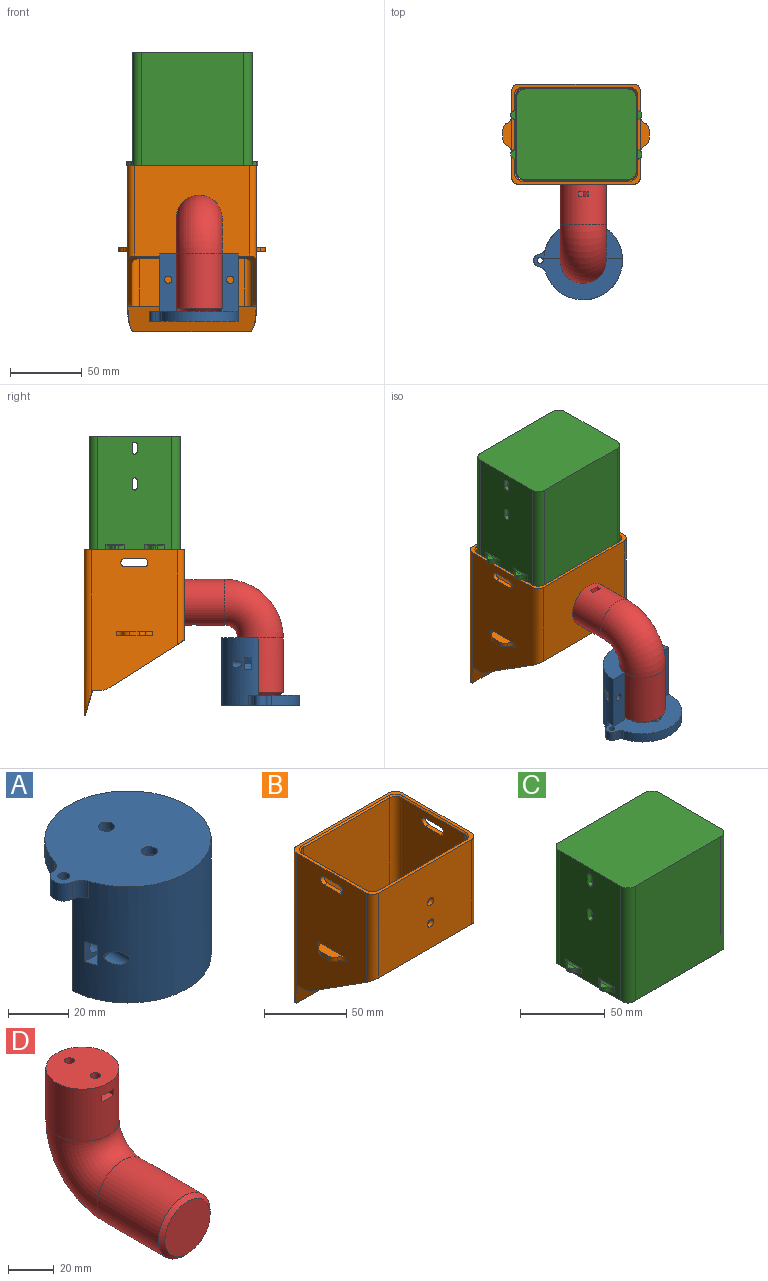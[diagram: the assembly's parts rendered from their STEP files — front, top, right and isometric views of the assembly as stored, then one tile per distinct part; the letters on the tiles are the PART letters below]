
ASSEMBLY  parts=4 mates=7
PART A: 33 faces, bbox 62x55x47 mm
  f0: cylinder r=27.5mm len=55mm, axis (0,0,-1), area 4287.3mm2, adj f1,f2,f6,f7,f8,f9,f10,f17
  f1: cylinder r=2.6mm len=8.99mm, axis (0,1,0), area 95.2mm2, adj f0,f25
  f2: cylinder r=2.6mm len=8.99mm, axis (0,1,0), area 95.1mm2, adj f0,f19
  f3: cylinder r=2.65mm len=5.3mm, axis (0,0,-1), area 50mm2, adj f8,f14
  f4: cylinder r=2.65mm len=5.3mm, axis (0,0,-1), area 50mm2, adj f8,f12
  f5: cylinder r=16mm len=40mm, axis (0,0,-1), area 1890.4mm2, adj f6,f7,f9,f10
  f6: plane 54.92x26mm, normal (0,0,-1), area 751.3mm2, adj f0,f5,f9,f10
  f7: plane 62x43.5mm, normal (0,0,-1), area 1446.6mm2, adj f0,f5,f9,f10,f11,f13,f29,f30
  f8: plane 62x55mm, normal (0,0,1), area 2379.9mm2, adj f0,f3,f4,f29,f30,f31,f32
  f9: plane 40x11.53mm, normal (0,1,0), area 439.9mm2, adj f0,f5,f6,f7,f16
  f10: plane 40x11.53mm, normal (0,1,0), area 439.9mm2, adj f0,f5,f6,f7,f15
  f11: cylinder r=6mm len=12mm, axis (0,0,-1), area 150.8mm2, adj f7,f12
  f12: plane 12x12mm, normal (0,0,-1), area 91mm2, adj f4,f11
  f13: cylinder r=6mm len=12mm, axis (0,0,-1), area 150.8mm2, adj f7,f14
  f14: plane 12x12mm, normal (0,0,-1), area 91mm2, adj f3,f13
  f15: cylinder r=2.6mm len=5.2mm, axis (0,1,0), area 81.7mm2, adj f10,f20
  f16: cylinder r=2.6mm len=5.2mm, axis (0,1,0), area 81.7mm2, adj f9,f26
  f17: plane 7.38x4.3mm, normal (0,0,-1), area 28.9mm2, adj f0,f19,f20,f21
  f18: plane 7.38x4.3mm, normal (0,0,1), area 28.9mm2, adj f0,f19,f20,f22
  f19: plane 8.3x8.15mm, normal (0,1,0), area 36.8mm2, adj f0,f2,f17,f18,f21,f22
  f20: plane 9.73x8.15mm, normal (0,-1,0), area 48.5mm2, adj f0,f15,f17,f18,f21,f22
  f21: plane 4.3x4.08mm, normal (-0.87,0,-0.5), area 20.2mm2, adj f17,f19,f20,f22
  f22: plane 4.3x4.08mm, normal (-0.87,0,0.5), area 20.2mm2, adj f18,f19,f20,f21
  f23: plane 7.38x4.3mm, normal (0,0,-1), area 28.9mm2, adj f0,f25,f26,f28
  f24: plane 7.38x4.3mm, normal (0,0,1), area 28.9mm2, adj f0,f25,f26,f27
  f25: plane 8.3x8.15mm, normal (0,1,0), area 36.8mm2, adj f0,f1,f23,f24,f27,f28
  f26: plane 9.73x8.15mm, normal (0,-1,0), area 48.5mm2, adj f0,f16,f23,f24,f27,f28
  f27: plane 4.3x4.08mm, normal (0.87,0,0.5), area 20.2mm2, adj f24,f25,f26,f28
  f28: plane 4.3x4.08mm, normal (0.87,0,-0.5), area 20.2mm2, adj f23,f25,f26,f27
  f29: cylinder r=4.5mm len=8.94mm, axis (0,0,-1), area 91.6mm2, adj f7,f8,f31,f32
  f30: cylinder r=2mm len=7mm, axis (0,0,-1), area 88mm2, adj f7,f8
  f31: cylinder r=5mm len=7mm, axis (0,0,1), area 40.6mm2, adj f0,f7,f8,f29
  f32: cylinder r=5mm len=7mm, axis (0,0,1), area 40.6mm2, adj f0,f7,f8,f29
PART B: 61 faces, bbox 103.3x71.3x117.4 mm
  f0: plane 97x54mm, normal (-1,0,0), area 4428.1mm2, adj f5,f11,f18,f19,f22,f33,f34,f35
  f1: plane 100.31x60mm, normal (1,0,0), area 4903.3mm2, adj f5,f10,f11,f14,f17,f22,f26,f33
  f2: plane 100.31x60mm, normal (-1,0,0), area 4903.3mm2, adj f4,f10,f11,f15,f16,f23,f30,f31
  f3: plane 97x54mm, normal (1,0,0), area 4428.1mm2, adj f4,f11,f20,f21,f23,f31,f32,f37
  f4: plane 6.39x3.42mm, normal (0,0,-1), area 18.6mm2, adj f2,f3,f13,f21,f23,f30
  f5: plane 6.39x3.42mm, normal (0,0,-1), area 18.6mm2, adj f0,f1,f13,f18,f22,f26
  f6: plane 80x63mm, normal (0,-1,0), area 4992.5mm2, adj f10,f11,f16,f17,f24,f25
  f7: plane 97x74mm, normal (0,-1,0), area 7178mm2, adj f12,f18,f21,f46
  f8: plane 74x63.91mm, normal (0,1,0), area 4681.8mm2, adj f11,f19,f20,f24,f25,f39
  f9: plane 116x80mm, normal (0,1,0), area 9280mm2, adj f10,f14,f15,f28
  f10: plane 90x70mm, normal (0,0,1), area 633.4mm2, adj f1,f2,f6,f9,f14,f15,f16,f17
  f11: plane 91.34x53.88mm, normal (0,-0.54,-0.84), area 672.4mm2, adj f0,f1,f2,f3,f6,f8,f16,f17
  f12: plane 83.17x3mm, normal (0,0,1), area 241.8mm2, adj f7,f13,f18,f21
  f13: plane 89.43x18.1mm, normal (0,-0.96,-0.29), area 1655.1mm2, adj f4,f5,f12,f26,f27,f28,f29,f30
  f14: cylinder r=5mm len=116mm, axis (0,0,1), area 849.5mm2, adj f1,f9,f10,f27
  f15: cylinder r=5mm len=116mm, axis (0,0,-1), area 849.5mm2, adj f2,f9,f10,f29
  f16: cylinder r=5mm len=66.18mm, axis (0,0,1), area 507.3mm2, adj f2,f6,f10,f11
  f17: cylinder r=5mm len=66.18mm, axis (0,0,-1), area 507.3mm2, adj f1,f6,f10,f11
  f18: cylinder r=5mm len=97mm, axis (0,0,-1), area 761.8mm2, adj f0,f5,f7,f12,f44
  f19: cylinder r=5mm len=67.09mm, axis (0,0,1), area 514.4mm2, adj f0,f8,f11,f40
  f20: cylinder r=5mm len=67.09mm, axis (0,0,-1), area 514.4mm2, adj f3,f8,f11,f41
  f21: cylinder r=5mm len=97mm, axis (0,0,1), area 761.8mm2, adj f3,f4,f7,f12,f45
  f22: cylinder r=10mm len=5.37mm, axis (-1,0,0), area 17mm2, adj f0,f1,f5,f11
  f23: cylinder r=10mm len=5.37mm, axis (-1,0,0), area 17mm2, adj f2,f3,f4,f11
  f24: cylinder r=2.75mm len=5.5mm, axis (0,-1,0), area 51.8mm2, adj f6,f8
  f25: cylinder r=2.75mm len=5.5mm, axis (0,-1,0), area 51.8mm2, adj f6,f8
  f26: plane 2.4x1mm, normal (0.71,-0.68,-0.2), area 1mm2, adj f1,f5,f13,f27
  f27: bspline ~15.77x5.28mm, area 9.1mm2, adj f13,f14,f26,f28
  f28: plane 80x0.57mm, normal (0,0.15,-0.99), area 46.5mm2, adj f9,f13,f27,f29
  f29: bspline ~15.77x5.28mm, area 9.1mm2, adj f13,f15,f28,f30
  f30: plane 2.4x1mm, normal (-0.71,-0.68,-0.2), area 1mm2, adj f2,f4,f13,f29
  f31: plane 13x3mm, normal (0,0,1), area 39mm2, adj f2,f3,f37,f38
  f32: plane 13x3mm, normal (0,0,-1), area 39mm2, adj f2,f3,f37,f38
  f33: plane 13x3mm, normal (0,0,-1), area 39mm2, adj f0,f1,f35,f36
  f34: plane 13x3mm, normal (0,0,1), area 39mm2, adj f0,f1,f35,f36
  f35: cylinder r=3mm len=6mm, axis (-1,0,0), area 28.3mm2, adj f0,f1,f33,f34
  f36: cylinder r=3mm len=6mm, axis (1,0,0), area 28.3mm2, adj f0,f1,f33,f34
  f37: cylinder r=3mm len=6mm, axis (-1,0,0), area 28.3mm2, adj f2,f3,f31,f32
  f38: cylinder r=3mm len=6mm, axis (-1,0,0), area 28.3mm2, adj f2,f3,f31,f32
  f39: plane 74x1mm, normal (0,0.71,0.71), area 104.7mm2, adj f8,f10,f40,f41
  f40: cone r=6mm half-angle=45deg, axis (0,0,1), area 12.2mm2, adj f10,f19,f39,f42
  f41: cone r=6mm half-angle=45deg, axis (0,0,1), area 12.2mm2, adj f10,f20,f39,f43
  f42: plane 54x1mm, normal (-0.71,0,0.71), area 76.4mm2, adj f0,f10,f40,f44
  f43: plane 54x1mm, normal (0.71,0,0.71), area 76.4mm2, adj f3,f10,f41,f45
  f44: cone r=6mm half-angle=45deg, axis (0,0,1), area 12.2mm2, adj f10,f18,f42,f46
  f45: cone r=6mm half-angle=45deg, axis (0,0,1), area 12.2mm2, adj f10,f21,f43,f46
  f46: plane 74x1mm, normal (0,-0.71,0.71), area 104.7mm2, adj f7,f10,f44,f45
  f47: plane 6.67x3mm, normal (-1,0,0), area 20mm2, adj f48,f49,f52,f53
  f48: plane 25x6mm, normal (0,0,1), area 95mm2, adj f2,f47,f50,f51,f52,f53
  f49: plane 25x6mm, normal (0,0,-1), area 95mm2, adj f2,f47,f50,f51,f52,f53
  f50: cylinder r=5mm len=4.58mm, axis (0,0,1), area 17.4mm2, adj f2,f48,f49,f52
  f51: cylinder r=5mm len=4.58mm, axis (0,0,-1), area 17.4mm2, adj f2,f48,f49,f53
  f52: cylinder r=5mm len=4.58mm, axis (0,0,1), area 17.4mm2, adj f47,f48,f49,f50
  f53: cylinder r=5mm len=4.58mm, axis (0,0,-1), area 17.4mm2, adj f47,f48,f49,f51
  f54: plane 6.67x3mm, normal (1,0,0), area 20mm2, adj f55,f56,f59,f60
  f55: plane 25x6mm, normal (0,0,1), area 95mm2, adj f1,f54,f57,f58,f59,f60
  f56: plane 25x6mm, normal (0,0,-1), area 95mm2, adj f1,f54,f57,f58,f59,f60
  f57: cylinder r=5mm len=4.58mm, axis (0,0,1), area 17.4mm2, adj f1,f55,f56,f59
  f58: cylinder r=5mm len=4.58mm, axis (0,0,-1), area 17.4mm2, adj f1,f55,f56,f60
  f59: cylinder r=5mm len=4.58mm, axis (0,0,1), area 17.4mm2, adj f54,f55,f56,f57
  f60: cylinder r=5mm len=4.58mm, axis (0,0,-1), area 17.4mm2, adj f54,f55,f56,f58
PART C: 75 faces, bbox 91.5x63.5x84.5 mm
  f0: plane 82.5x51.5mm, normal (1,0,0), area 4084.1mm2, adj f10,f15,f18,f27,f28,f29,f30,f31
  f1: plane 82.5x51.5mm, normal (-1,0,0), area 4084.1mm2, adj f10,f16,f17,f19,f20,f21,f22,f23
  f2: plane 81.5x49.5mm, normal (1,0,0), area 3980mm2, adj f8,f9,f11,f14,f19,f20,f21,f22
  f3: plane 81.5x69.5mm, normal (0,-1,0), area 5664.3mm2, adj f8,f9,f11,f12
  f4: plane 81.5x49.5mm, normal (-1,0,0), area 3980mm2, adj f8,f9,f12,f13,f27,f28,f29,f30
  f5: plane 82.5x71.5mm, normal (0,1,0), area 5898.7mm2, adj f10,f15,f16,f67
  f6: plane 82.5x71.5mm, normal (0,-1,0), area 5898.7mm2, adj f10,f17,f18,f74
  f7: plane 81.5x69.5mm, normal (0,1,0), area 5664.3mm2, adj f8,f9,f13,f14
  f8: plane 79.5x59.5mm, normal (0,0,-1), area 274mm2, adj f2,f3,f4,f7,f11,f12,f13,f14
  f9: plane 77.5x57.5mm, normal (0,0,-1), area 4442.5mm2, adj f2,f3,f4,f7,f11,f12,f13,f14
  f10: plane 83.5x63.5mm, normal (0,0,1), area 5271.3mm2, adj f0,f1,f5,f6,f15,f16,f17,f18
  f11: cylinder r=4mm len=81.5mm, axis (0,0,1), area 512.1mm2, adj f2,f3,f8,f9
  f12: cylinder r=4mm len=81.5mm, axis (0,0,-1), area 512.1mm2, adj f3,f4,f8,f9
  f13: cylinder r=4mm len=81.5mm, axis (0,0,1), area 512.1mm2, adj f4,f7,f8,f9
  f14: cylinder r=4mm len=81.5mm, axis (0,0,-1), area 512.1mm2, adj f2,f7,f8,f9
  f15: cylinder r=6mm len=82.5mm, axis (0,0,1), area 777.5mm2, adj f0,f5,f10,f68
  f16: cylinder r=6mm len=82.5mm, axis (0,0,-1), area 777.5mm2, adj f1,f5,f10,f69
  f17: cylinder r=6mm len=82.5mm, axis (0,0,1), area 777.5mm2, adj f1,f6,f10,f73
  f18: cylinder r=6mm len=82.5mm, axis (0,0,-1), area 777.5mm2, adj f0,f6,f10,f72
  f19: plane 5x3mm, normal (0,1,0), area 15mm2, adj f1,f2,f20,f22
  f20: cylinder r=1.75mm len=3.5mm, axis (1,0,0), area 16.5mm2, adj f1,f2,f19,f21
  f21: plane 5x3mm, normal (0,-1,0), area 15mm2, adj f1,f2,f20,f22
  f22: cylinder r=1.75mm len=3.5mm, axis (1,0,0), area 16.5mm2, adj f1,f2,f19,f21
  f23: cylinder r=1.75mm len=3.5mm, axis (1,0,0), area 16.5mm2, adj f1,f2,f24,f26
  f24: plane 5x3mm, normal (0,1,0), area 15mm2, adj f1,f2,f23,f25
  f25: cylinder r=1.75mm len=3.5mm, axis (1,0,0), area 16.5mm2, adj f1,f2,f24,f26
  f26: plane 5x3mm, normal (0,-1,0), area 15mm2, adj f1,f2,f23,f25
  f27: cylinder r=1.75mm len=3.5mm, axis (1,0,0), area 16.5mm2, adj f0,f4,f28,f30
  f28: plane 5x3mm, normal (0,-1,0), area 15mm2, adj f0,f4,f27,f29
  f29: cylinder r=1.75mm len=3.5mm, axis (1,0,0), area 16.5mm2, adj f0,f4,f28,f30
  f30: plane 5x3mm, normal (0,1,0), area 15mm2, adj f0,f4,f27,f29
  f31: plane 5x3mm, normal (0,-1,0), area 15mm2, adj f0,f4,f32,f34
  f32: cylinder r=1.75mm len=3.5mm, axis (1,0,0), area 16.5mm2, adj f0,f4,f31,f33
  f33: plane 5x3mm, normal (0,1,0), area 15mm2, adj f0,f4,f32,f34
  f34: cylinder r=1.75mm len=3.5mm, axis (1,0,0), area 16.5mm2, adj f0,f4,f31,f33
  f35: plane 7.8x3mm, normal (0,0,1), area 15.5mm2, adj f37,f38,f39,f40,f49,f50
  f36: plane 13.8x4mm, normal (0,0,-1), area 25.2mm2, adj f1,f37,f38,f39,f49,f50
  f37: plane 3x1.15mm, normal (-1,0,0), area 3.4mm2, adj f35,f36,f49,f50
  f38: cylinder r=5mm len=4.52mm, axis (0,0,-1), area 18.2mm2, adj f1,f35,f36,f40,f49
  f39: cylinder r=5mm len=4.52mm, axis (0,0,-1), area 18.2mm2, adj f1,f35,f36,f40,f50
  f40: cylinder r=1mm len=13.8mm, axis (0,-1,0), area 16.6mm2, adj f1,f35,f38,f39
  f41: plane 13.8x4mm, normal (0,0,-1), area 25.2mm2, adj f1,f43,f44,f45,f47,f48
  f42: plane 7.8x3mm, normal (0,0,1), area 15.5mm2, adj f43,f44,f45,f46,f47,f48
  f43: plane 3x1.15mm, normal (-1,0,0), area 3.4mm2, adj f41,f42,f47,f48
  f44: cylinder r=5mm len=4.52mm, axis (0,0,-1), area 18.2mm2, adj f1,f41,f42,f46,f47
  f45: cylinder r=5mm len=4.52mm, axis (0,0,-1), area 18.2mm2, adj f1,f41,f42,f46,f48
  f46: cylinder r=1mm len=13.8mm, axis (0,-1,0), area 16.6mm2, adj f1,f42,f44,f45
  f47: cylinder r=2mm len=3mm, axis (0,0,-1), area 6.8mm2, adj f41,f42,f43,f44
  f48: cylinder r=2mm len=3mm, axis (0,0,-1), area 6.8mm2, adj f41,f42,f43,f45
  f49: cylinder r=2mm len=3mm, axis (0,0,-1), area 6.8mm2, adj f35,f36,f37,f38
  f50: cylinder r=2mm len=3mm, axis (0,0,-1), area 6.8mm2, adj f35,f36,f37,f39
  f51: plane 13.8x4mm, normal (0,0,-1), area 25.2mm2, adj f0,f53,f54,f55,f65,f66
  f52: plane 7.8x3mm, normal (0,0,1), area 15.5mm2, adj f53,f54,f55,f56,f65,f66
  f53: plane 3x1.15mm, normal (1,0,0), area 3.4mm2, adj f51,f52,f65,f66
  f54: cylinder r=5mm len=4.52mm, axis (0,0,-1), area 18.2mm2, adj f0,f51,f52,f56,f65
  f55: cylinder r=5mm len=4.52mm, axis (0,0,-1), area 18.2mm2, adj f0,f51,f52,f56,f66
  f56: cylinder r=1mm len=13.8mm, axis (0,-1,0), area 16.6mm2, adj f0,f52,f54,f55
  f57: plane 7.8x3mm, normal (0,0,1), area 15.5mm2, adj f59,f60,f61,f62,f63,f64
  f58: plane 13.8x4mm, normal (0,0,-1), area 25.2mm2, adj f0,f59,f60,f61,f63,f64
  f59: plane 3x1.15mm, normal (1,0,0), area 3.4mm2, adj f57,f58,f63,f64
  f60: cylinder r=5mm len=4.52mm, axis (0,0,-1), area 18.2mm2, adj f0,f57,f58,f62,f63
  f61: cylinder r=5mm len=4.52mm, axis (0,0,-1), area 18.2mm2, adj f0,f57,f58,f62,f64
  f62: cylinder r=1mm len=13.8mm, axis (0,-1,0), area 16.6mm2, adj f0,f57,f60,f61
  f63: cylinder r=2mm len=3mm, axis (0,0,-1), area 6.8mm2, adj f57,f58,f59,f60
  f64: cylinder r=2mm len=3mm, axis (0,0,-1), area 6.8mm2, adj f57,f58,f59,f61
  f65: cylinder r=2mm len=3mm, axis (0,0,-1), area 6.8mm2, adj f51,f52,f53,f54
  f66: cylinder r=2mm len=3mm, axis (0,0,-1), area 6.8mm2, adj f51,f52,f53,f55
  f67: plane 71.5x2mm, normal (0,0.71,-0.71), area 202.2mm2, adj f5,f8,f68,f69
  f68: cone r=4mm half-angle=45deg, axis (0,0,1), area 22.2mm2, adj f8,f15,f67,f70
  f69: cone r=4mm half-angle=45deg, axis (0,0,1), area 22.2mm2, adj f8,f16,f67,f71
  f70: plane 51.5x2mm, normal (0.71,0,-0.71), area 145.7mm2, adj f0,f8,f68,f72
  f71: plane 51.5x2mm, normal (-0.71,0,-0.71), area 145.7mm2, adj f1,f8,f69,f73
  f72: cone r=4mm half-angle=45deg, axis (0,0,1), area 22.2mm2, adj f8,f18,f70,f74
  f73: cone r=4mm half-angle=45deg, axis (0,0,1), area 22.2mm2, adj f8,f17,f71,f74
  f74: plane 71.5x2mm, normal (0,-0.71,-0.71), area 202.2mm2, adj f6,f8,f72,f73
PART D: 24 faces, bbox 32x84.4x72.4 mm
  f0: cylinder r=16mm len=32mm, axis (0,0,-1), area 2765.8mm2, adj f1,f2,f5,f6,f7,f8,f11,f12
  f1: plane 32x32mm, normal (0,0,1), area 775.2mm2, adj f0,f14,f17
  f2: plane 9.66x3.4mm, normal (-1,0,0), area 32.8mm2, adj f0,f3,f6,f7
  f3: plane 3.58x3.4mm, normal (-0.5,-0.87,0), area 14mm2, adj f2,f4,f6,f7
  f4: plane 3.58x3.4mm, normal (0.5,-0.87,0), area 14mm2, adj f3,f5,f6,f7
  f5: plane 9.66x3.4mm, normal (1,0,0), area 32.8mm2, adj f0,f4,f6,f7
  f6: plane 12.13x7.15mm, normal (0,0,1), area 63.9mm2, adj f0,f2,f3,f4,f5,f18
  f7: plane 12.13x7.15mm, normal (0,0,-1), area 63.9mm2, adj f0,f2,f3,f4,f5,f17
  f8: plane 9.66x3.4mm, normal (1,0,0), area 32.8mm2, adj f0,f9,f12,f13
  f9: plane 3.58x3.4mm, normal (0.5,0.87,0), area 14mm2, adj f8,f10,f12,f13
  f10: plane 3.58x3.4mm, normal (-0.5,0.87,0), area 14mm2, adj f9,f11,f12,f13
  f11: plane 9.66x3.4mm, normal (-1,0,0), area 32.8mm2, adj f0,f10,f12,f13
  f12: plane 12.13x7.15mm, normal (0,0,1), area 63.9mm2, adj f0,f8,f9,f10,f11,f15
  f13: plane 12.13x7.15mm, normal (0,0,-1), area 63.9mm2, adj f0,f8,f9,f10,f11,f14
  f14: cylinder r=2.15mm len=5mm, axis (0,0,-1), area 67.5mm2, adj f1,f13
  f15: cylinder r=2.15mm len=6.6mm, axis (0,0,-1), area 89.2mm2, adj f12,f16
  f16: plane 4.3x4.3mm, normal (0,0,1), area 14.5mm2, adj f15
  f17: cylinder r=2.15mm len=5mm, axis (0,0,-1), area 67.5mm2, adj f1,f7
  f18: cylinder r=2.15mm len=6.6mm, axis (0,0,-1), area 89.2mm2, adj f6,f19
  f19: plane 4.3x4.3mm, normal (0,0,1), area 14.5mm2, adj f18
  f20: plane 28x28mm, normal (0,-1,0), area 615.8mm2, adj f23
  f21: torus R=25mm, axis (-1,0,0), area 3947.8mm2, adj f0,f22
  f22: cylinder r=16mm len=38mm, axis (0,-1,0), area 3820.2mm2, adj f21,f23
  f23: cone r=14mm half-angle=45deg, axis (0,1,0), area 266.6mm2, adj f20,f22
PLACE A rot(axis=(1,0,0),180deg) t=(5.62,-95.32,-54.25)mm
PLACE B t=(0.62,-7.32,-0.65)mm fixed
PLACE C t=(0.87,-7.57,2.35)mm
PLACE D rot(axis=(0,0.71,0.71),180deg) t=(5.62,-70.32,-29.25)mm
MATE planar C.f64 <-> B.f10  axis (0,0,-1) through (44.62,-20.75,7.35)mm
MATE revolute B.f25 <-> D.f14  axis (0,-1,0) through (5.62,-42.32,-21.25)mm
MATE cylindrical B.f24 <-> D.f17  axis (0,-1,0) through (5.62,-42.32,-37.25)mm
MATE parallel A.f1 <-> B.f6  axis (0,-1,0) through (27.31,-93.82,-72.25)mm
MATE revolute A.f5 <-> D.f22  axis (0,0,1) through (5.62,-95.32,-94.25)mm
MATE planar C.f0 <-> B.f0  axis (1,0,0) through (42.62,-7.57,46.31)mm
MATE planar C.f6 <-> B.f8  axis (0,-1,0) through (0.87,-39.32,45.6)mm
